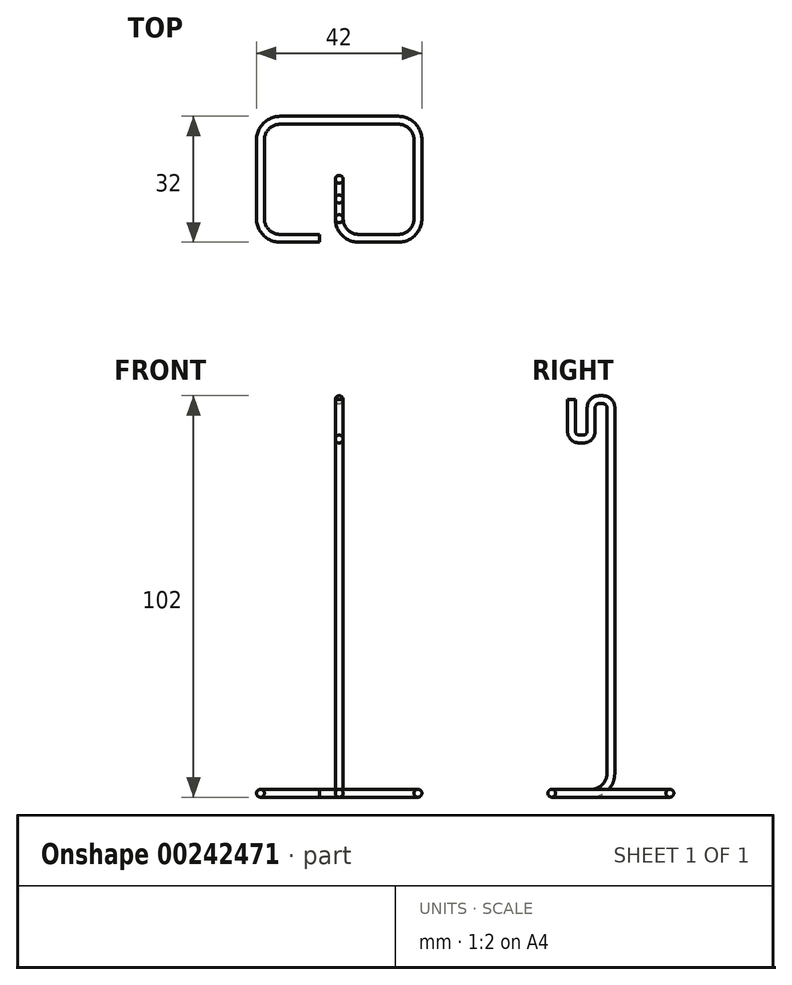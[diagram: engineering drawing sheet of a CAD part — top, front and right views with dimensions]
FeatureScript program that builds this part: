
annotation { "Feature Type Name" : "Feature", "Feature Type Description" : "" }
export const myFeature = defineFeature(function(context is Context, id is Id, definition is map)
    precondition{}
    {
        {
            var Q0;
            Q0=qCreatedBy(makeId("Right.planeOp"),FACE);
            var sketch = newSketch(context, id + "F0", { "sketchPlane" : qUnion([Q0])});
            skLineSegment(sketch, "E0", {"start": v(-17.15, 58.27) * mm, "end": v(-17.15, 50.27) * mm});
            skLineSegment(sketch, "E1", {"start": v(-15.15, 48.27) * mm, "end": v(-14.15, 48.27) * mm});
            skLineSegment(sketch, "E2", {"start": v(-12.15, 50.27) * mm, "end": v(-12.15, 56.27) * mm});
            skLineSegment(sketch, "E3", {"start": v(-10.15, 58.27) * mm, "end": v(-9.15, 58.27) * mm});
            skLineSegment(sketch, "E4", {"start": v(-7.15, 56.27) * mm, "end": v(-7.15, -36.73) * mm});
            skPoint(sketch, "E5.visualSharp", {"position": v(-17.15, 48.27) * mm});
            skArc(sketch, "E5.filletArc", {"start": v(-17.15, 50.27) * mm, "mid": v(-16.57, 48.86) * mm, "end": v(-15.15, 48.27) * mm});
            skPoint(sketch, "E6.visualSharp", {"position": v(-12.15, 48.27) * mm});
            skArc(sketch, "E6.filletArc", {"start": v(-14.15, 48.27) * mm, "mid": v(-12.74, 48.86) * mm, "end": v(-12.15, 50.27) * mm});
            skPoint(sketch, "E7.visualSharp", {"position": v(-12.15, 58.27) * mm});
            skArc(sketch, "E7.filletArc", {"start": v(-10.15, 58.27) * mm, "mid": v(-11.57, 57.69) * mm, "end": v(-12.15, 56.27) * mm});
            skPoint(sketch, "E8.visualSharp", {"position": v(-7.15, 58.27) * mm});
            skArc(sketch, "E8.filletArc", {"start": v(-7.15, 56.27) * mm, "mid": v(-7.74, 57.69) * mm, "end": v(-9.15, 58.27) * mm});
            skLineSegment(sketch, "E9", {"start": v(-12.15, -41.73) * mm, "end": v(-17.15, -41.73) * mm});
            skPoint(sketch, "E10.visualSharp", {"position": v(-7.15, -41.73) * mm});
            skArc(sketch, "E10.filletArc", {"start": v(-12.15, -41.73) * mm, "mid": v(-8.62, -40.26) * mm, "end": v(-7.15, -36.73) * mm});
            skSolve(sketch);
        }
        {
            var Q0;
            Q0=qCreatedBy(makeId("Top.planeOp"),FACE);
            var Q1;
            Q1=sQuery(id+"F0.wireOp",VERTEX,"E0.start");
            cPlane(context, id + "F1", {"entities" : qUnion([Q0, Q1]), "cplaneType" : CPlaneType.PLANE_POINT, "offset" : 25 * mm, "width" : 150 * mm, "height" : 150 * mm});
        }
        {
            var Q0;
            Q0=qCreatedBy(id+"F1.planeOp",FACE);
            var sketch = newSketch(context, id + "F2", { "sketchPlane" : qUnion([Q0])});
            skCircle(sketch, "E11", {"center": v(0, -17.15) * mm, "radius": 1 * mm});
            skSolve(sketch);
        }
        {
            var Q0;
            Q0=makeQuery(id+"F2.imprint","IMPRINT",FACE,{"disambiguationData":[TD([[makeQuery(id+"F2.imprint","IMPRINT",EDGE,{"derivedFrom":sQuery(id+"F2.wireOp",EDGE,"E11")}),1.0]])]});
            var Q1;
            Q1=sQuery(id+"F0.wireOp",EDGE,"E0");
            var Q2;
            Q2=sQuery(id+"F0.wireOp",EDGE,"E5.filletArc");
            var Q3;
            Q3=sQuery(id+"F0.wireOp",EDGE,"E6.filletArc");
            var Q4;
            Q4=sQuery(id+"F0.wireOp",EDGE,"E1");
            var Q5;
            Q5=sQuery(id+"F0.wireOp",EDGE,"E2");
            var Q6;
            Q6=sQuery(id+"F0.wireOp",EDGE,"E7.filletArc");
            var Q7;
            Q7=sQuery(id+"F0.wireOp",EDGE,"E3");
            var Q8;
            Q8=sQuery(id+"F0.wireOp",EDGE,"E8.filletArc");
            var Q9;
            Q9=sQuery(id+"F0.wireOp",EDGE,"E4");
            var Q10;
            Q10=sQuery(id+"F0.wireOp",EDGE,"E10.filletArc");
            var Q11;
            Q11=sQuery(id+"F0.wireOp",EDGE,"E9");
            sweep(context, id + "F3", {"profiles" : qUnion([Q0]), "path" : qUnion([Q1, Q2, Q3, Q4, Q5, Q6, Q7, Q8, Q9, Q10, Q11])});
        }
        {
            var Q0;
            Q0=qCreatedBy(makeId("Top.planeOp"),FACE);
            var Q1;
            Q1=sQuery(id+"F0.wireOp",VERTEX,"E9.end");
            cPlane(context, id + "F4", {"entities" : qUnion([Q0, Q1]), "cplaneType" : CPlaneType.PLANE_POINT, "offset" : 25 * mm, "width" : 150 * mm, "height" : 150 * mm});
        }
        {
            var Q0;
            Q0=qCreatedBy(id+"F4.planeOp",FACE);
            var sketch = newSketch(context, id + "F5", { "sketchPlane" : qUnion([Q0])});
            skPoint(sketch, "E12.0", {"position": v(0, -17.15) * mm});
            skLineSegment(sketch, "E13.bottom", {"start": v(15, -22.15) * mm, "end": v(5, -22.15) * mm});
            skLineSegment(sketch, "E13.top", {"start": v(15, 7.85) * mm, "end": v(-15, 7.85) * mm});
            skLineSegment(sketch, "E13.left", {"start": v(20, -17.15) * mm, "end": v(20, 2.85) * mm});
            skLineSegment(sketch, "E13.right", {"start": v(-20, -17.15) * mm, "end": v(-20, 2.85) * mm});
            skLineSegment(sketch, "E14", {"start": v(0, -17.15) * mm, "end": v(0, -17.15) * mm});
            skLineSegment(sketch, "E15.trimOffspring", {"start": v(-5, -22.15) * mm, "end": v(-15, -22.15) * mm});
            skPoint(sketch, "E16.visualSharp", {"position": v(-20, -22.15) * mm});
            skArc(sketch, "E16.filletArc", {"start": v(-20, -17.15) * mm, "mid": v(-18.54, -20.69) * mm, "end": v(-15, -22.15) * mm});
            skPoint(sketch, "E17.visualSharp", {"position": v(0, -22.15) * mm});
            skArc(sketch, "E17.filletArc", {"start": v(0, -17.15) * mm, "mid": v(1.46, -20.69) * mm, "end": v(5, -22.15) * mm});
            skPoint(sketch, "E18.visualSharp", {"position": v(-20, 7.85) * mm});
            skArc(sketch, "E18.filletArc", {"start": v(-15, 7.85) * mm, "mid": v(-18.54, 6.38) * mm, "end": v(-20, 2.85) * mm});
            skPoint(sketch, "E19.visualSharp", {"position": v(20, 7.85) * mm});
            skArc(sketch, "E19.filletArc", {"start": v(20, 2.85) * mm, "mid": v(18.54, 6.38) * mm, "end": v(15, 7.85) * mm});
            skPoint(sketch, "E20.visualSharp", {"position": v(20, -22.15) * mm});
            skArc(sketch, "E20.filletArc", {"start": v(15, -22.15) * mm, "mid": v(18.54, -20.69) * mm, "end": v(20, -17.15) * mm});
            skSolve(sketch);
        }
        {
            var Q0;
            Q0=makeQuery(id+"F3.opSweep","CAP_FACE",FACE,{"disambiguationData":[OSD([sQuery(id+"F0.wireOp",VERTEX,"E9.end"),sQuery(id+"F2.wireOp",EDGE,"E11")])],"isStart":false});
            var Q1;
            Q1=sQuery(id+"F5.wireOp",EDGE,"E17.filletArc");
            var Q2;
            Q2=sQuery(id+"F5.wireOp",EDGE,"E13.bottom");
            var Q3;
            Q3=sQuery(id+"F5.wireOp",EDGE,"E20.filletArc");
            var Q4;
            Q4=sQuery(id+"F5.wireOp",EDGE,"E13.left");
            var Q5;
            Q5=sQuery(id+"F5.wireOp",EDGE,"E19.filletArc");
            var Q6;
            Q6=sQuery(id+"F5.wireOp",EDGE,"E13.top");
            var Q7;
            Q7=sQuery(id+"F5.wireOp",EDGE,"E13.right");
            var Q8;
            Q8=sQuery(id+"F5.wireOp",EDGE,"E18.filletArc");
            var Q9;
            Q9=sQuery(id+"F5.wireOp",EDGE,"E16.filletArc");
            var Q10;
            Q10=sQuery(id+"F5.wireOp",EDGE,"E15.trimOffspring");
            sweep(context, id + "F6", {"operationType" : NewBodyOperationType.ADD, "profiles" : qUnion([Q0]), "path" : qUnion([Q1, Q2, Q3, Q4, Q5, Q6, Q7, Q8, Q9, Q10])});
        }
    });
